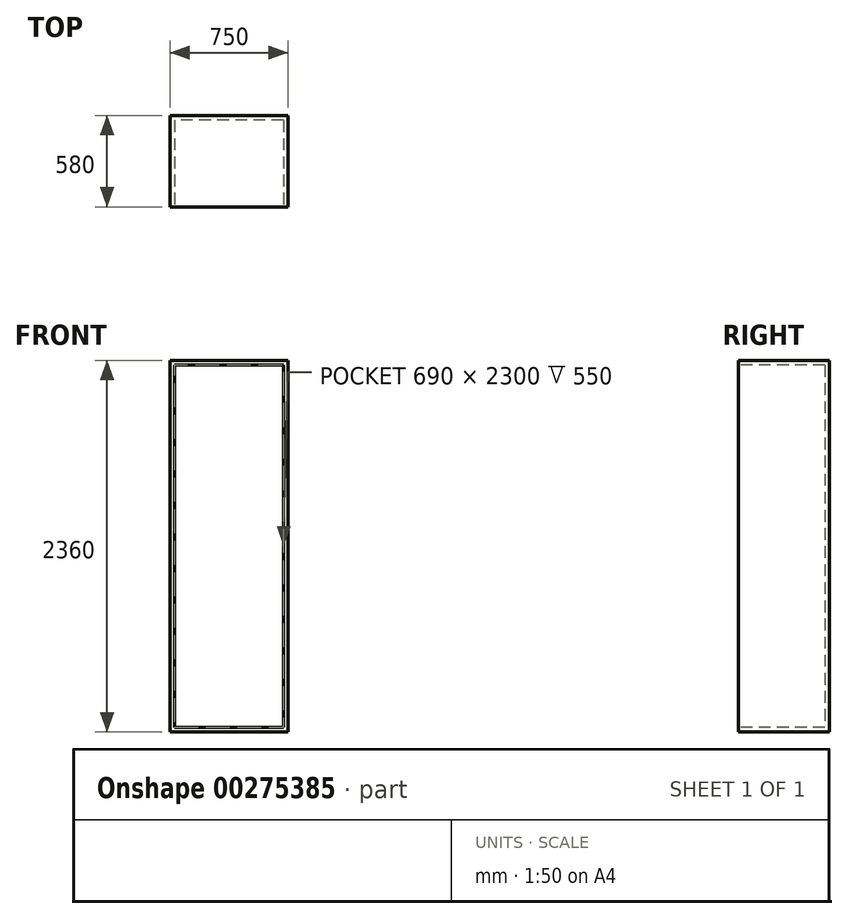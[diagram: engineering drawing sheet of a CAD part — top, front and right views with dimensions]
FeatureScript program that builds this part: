
annotation { "Feature Type Name" : "Feature", "Feature Type Description" : "" }
export const myFeature = defineFeature(function(context is Context, id is Id, definition is map)
    precondition{}
    {
        {
            var Q0;
            Q0=qCreatedBy(makeId("Top.planeOp"),FACE);
            var sketch = newSketch(context, id + "F0", { "sketchPlane" : qUnion([Q0])});
            skLineSegment(sketch, "E0.bottom", {"start": v(375, 290) * mm, "end": v(-375, 290) * mm});
            skLineSegment(sketch, "E0.top", {"start": v(375, -290) * mm, "end": v(-375, -290) * mm});
            skLineSegment(sketch, "E0.left", {"start": v(375, 290) * mm, "end": v(375, -290) * mm});
            skLineSegment(sketch, "E0.right", {"start": v(-375, 290) * mm, "end": v(-375, -290) * mm});
            skPoint(sketch, "E0.middle", {"position": v(0, 0) * mm});
            skSolve(sketch);
        }
        {
            var Q0;
            Q0 = qSketchRegion(id + "F0", true);
            extrude(context, id + "F1", {"entities" : qUnion([Q0]), "depth" : 2360 * mm});
        }
        {
            var Q0;
            Q0=makeQuery(id+"F1.opExtrude","SWEPT_FACE",FACE,{"disambiguationData":[OSD([sQuery(id+"F0.wireOp",EDGE,"E0.top")])]});
            shell(context, id + "F2", {"entities" : qUnion([Q0]), "thickness" : 30 * mm});
        }
    });
